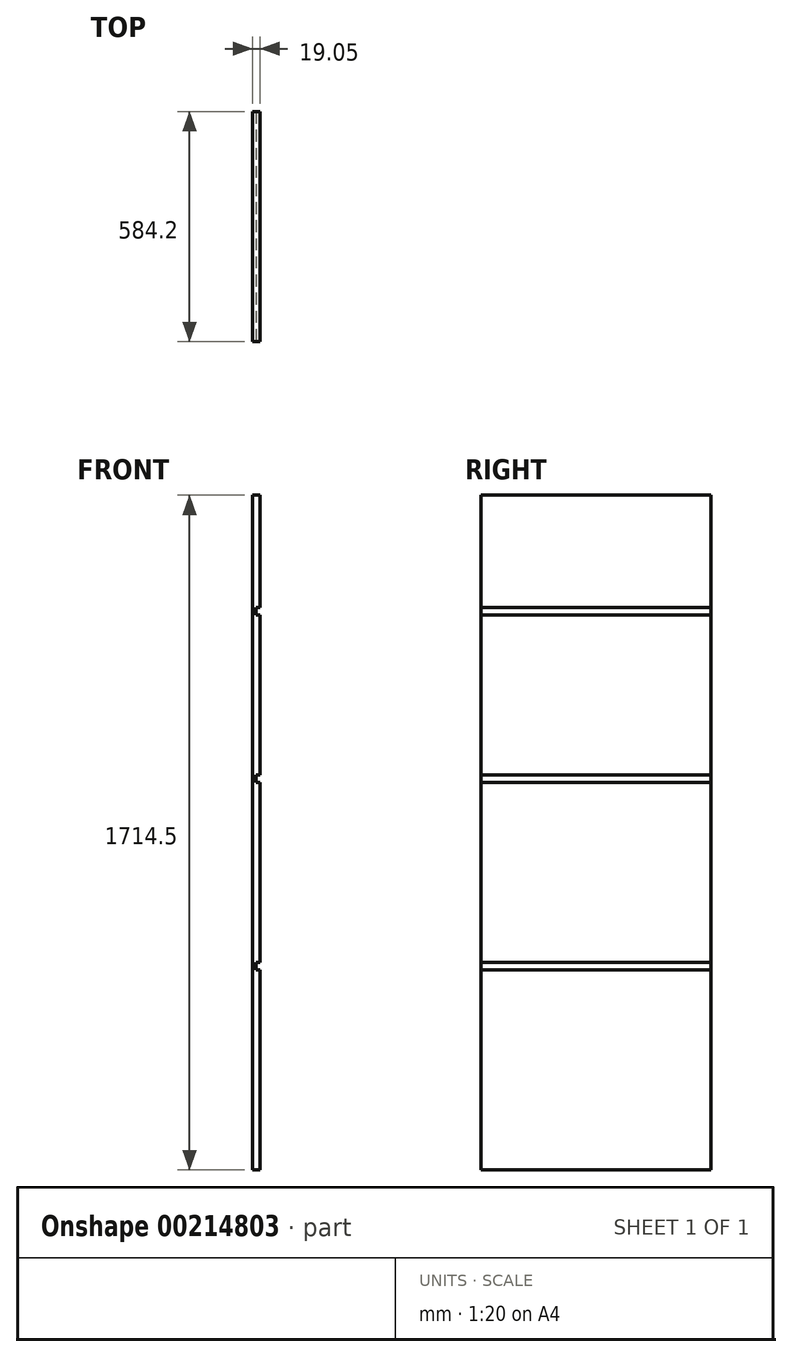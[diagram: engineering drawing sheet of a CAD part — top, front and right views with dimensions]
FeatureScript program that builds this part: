
annotation { "Feature Type Name" : "Feature", "Feature Type Description" : "" }
export const myFeature = defineFeature(function(context is Context, id is Id, definition is map)
    precondition{}
    {
        {
            var Q0;
            Q0=qCreatedBy(makeId("Right.planeOp"),FACE);
            var sketch = newSketch(context, id + "F0", { "sketchPlane" : qUnion([Q0])});
            skLineSegment(sketch, "E0.bottom", {"start": v(0, 0) * mm, "end": v(584.2, 0) * mm});
            skLineSegment(sketch, "E0.top", {"start": v(0, -1714.5) * mm, "end": v(584.2, -1714.5) * mm});
            skLineSegment(sketch, "E0.left", {"start": v(0, 0) * mm, "end": v(0, -1714.5) * mm});
            skLineSegment(sketch, "E0.right", {"start": v(584.2, 0) * mm, "end": v(584.2, -1714.5) * mm});
            skSolve(sketch);
        }
        {
            var Q0;
            Q0=makeQuery(id+"F0.imprint","IMPRINT",FACE,{"disambiguationData":[TD([[makeQuery(id+"F0.imprint","IMPRINT",EDGE,{"derivedFrom":sQuery(id+"F0.wireOp",EDGE,"E0.bottom")}),-1.0]])]});
            extrude(context, id + "F1", {"entities" : qUnion([Q0]), "depth" : 19.05 * mm});
        }
        {
            var Q0;
            Q0=makeQuery(id+"F1.opExtrude","SWEPT_FACE",FACE,{"disambiguationData":[OSD([sQuery(id+"F0.wireOp",EDGE,"E0.left")])]});
            var sketch = newSketch(context, id + "F2", { "sketchPlane" : qUnion([Q0])});
            skLineSegment(sketch, "E1.bottom", {"start": v(19.05, -1187.45) * mm, "end": v(9.53, -1187.45) * mm});
            skLineSegment(sketch, "E1.top", {"start": v(19.05, -1206.5) * mm, "end": v(9.53, -1206.5) * mm});
            skLineSegment(sketch, "E1.left", {"start": v(19.05, -1187.45) * mm, "end": v(19.05, -1206.5) * mm});
            skLineSegment(sketch, "E1.right", {"start": v(9.53, -1187.45) * mm, "end": v(9.53, -1206.5) * mm});
            skLineSegment(sketch, "E2.bottom", {"start": v(19.05, -711.2) * mm, "end": v(9.52, -711.2) * mm});
            skLineSegment(sketch, "E2.top", {"start": v(19.05, -730.25) * mm, "end": v(9.52, -730.25) * mm});
            skLineSegment(sketch, "E2.left", {"start": v(19.05, -711.2) * mm, "end": v(19.05, -730.25) * mm});
            skLineSegment(sketch, "E2.right", {"start": v(9.52, -711.2) * mm, "end": v(9.52, -730.25) * mm});
            skLineSegment(sketch, "E3.bottom", {"start": v(19.05, -285.75) * mm, "end": v(9.52, -285.75) * mm});
            skLineSegment(sketch, "E3.top", {"start": v(19.05, -304.8) * mm, "end": v(9.52, -304.8) * mm});
            skLineSegment(sketch, "E3.left", {"start": v(19.05, -285.75) * mm, "end": v(19.05, -304.8) * mm});
            skLineSegment(sketch, "E3.right", {"start": v(9.52, -285.75) * mm, "end": v(9.52, -304.8) * mm});
            skSolve(sketch);
        }
        {
            var Q0;
            Q0=makeQuery(id+"F2.imprint","IMPRINT",FACE,{"disambiguationData":[TD([[makeQuery(id+"F2.imprint","IMPRINT",EDGE,{"derivedFrom":sQuery(id+"F2.wireOp",EDGE,"E3.bottom")}),1.0]])]});
            var Q1;
            Q1=makeQuery(id+"F2.imprint","IMPRINT",FACE,{"disambiguationData":[TD([[makeQuery(id+"F2.imprint","IMPRINT",EDGE,{"derivedFrom":sQuery(id+"F2.wireOp",EDGE,"E2.bottom")}),1.0]])]});
            var Q2;
            Q2=makeQuery(id+"F2.imprint","IMPRINT",FACE,{"disambiguationData":[TD([[makeQuery(id+"F2.imprint","IMPRINT",EDGE,{"derivedFrom":sQuery(id+"F2.wireOp",EDGE,"E1.bottom")}),1.0]])]});
            extrude(context, id + "F3", {"entities" : qUnion([Q0, Q1, Q2]), "operationType" : NewBodyOperationType.REMOVE, "oppositeDirection" : true, "depth" : 584.2 * mm});
        }
    });
